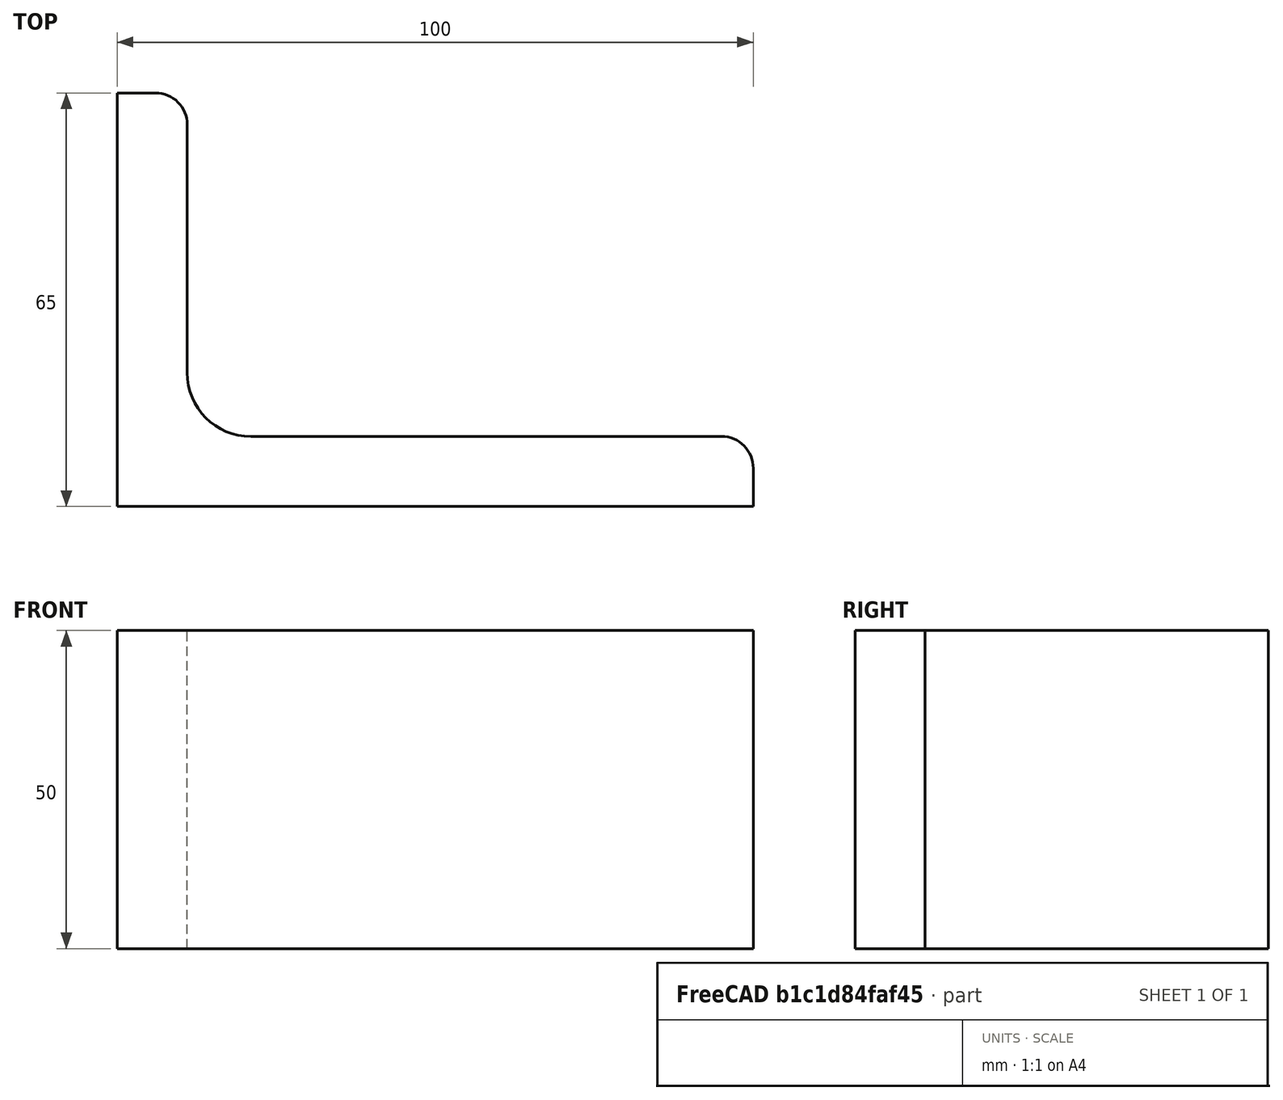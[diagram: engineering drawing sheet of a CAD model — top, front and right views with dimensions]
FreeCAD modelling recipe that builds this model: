
FCSTD DOCUMENT  (FreeCAD 0.15R4671 (Git))
Label: Angle Bar 100x65x11 EN10056 S235JR
License: All rights reserved
LicenseURL: http://en.wikipedia.org/wiki/All_rights_reserved
objects: Sketcher::SketchObject×1, Part::Extrusion×1
note: 2 computed .brp shape members not serialized (recipe doc carries the construction recipe); baked Part::Feature solids carry a one-line shape summary decoded from their .brp

FEATURE [Sketcher::SketchObject] Sketch
  sketch-geometry (9):
    g0: LineSegment StartX=0 StartY=0 StartZ=0 EndX=100 EndY=0 EndZ=0
    g1: LineSegment StartX=100 StartY=0 StartZ=0 EndX=100 EndY=6 EndZ=0
    g2: LineSegment StartX=95 StartY=11 StartZ=0 EndX=21 EndY=11 EndZ=0
    g3: LineSegment StartX=0 StartY=0 StartZ=0 EndX=0 EndY=65 EndZ=0
    g4: LineSegment StartX=0 StartY=65 StartZ=0 EndX=6 EndY=65 EndZ=0
    g5: LineSegment StartX=11 StartY=60 StartZ=0 EndX=11 EndY=21 EndZ=0
    g6: ArcOfCircle CenterX=21 CenterY=21 CenterZ=0 NormalX=0 NormalY=0 NormalZ=1 Radius=10 StartAngle=3.14159 EndAngle=4.71239
    g7: ArcOfCircle CenterX=6 CenterY=60 CenterZ=0 NormalX=0 NormalY=0 NormalZ=1 Radius=5 StartAngle=0 EndAngle=1.5708
    g8: ArcOfCircle CenterX=95 CenterY=6 CenterZ=0 NormalX=0 NormalY=0 NormalZ=1 Radius=5 StartAngle=0 EndAngle=1.5708
  constraints (23):
    c: Coincident(g0,g-1)
    c: Horizontal(g0)
    c: Coincident(g1,g0)
    c: Vertical(g1)
    c: Horizontal(g2)
    c: Coincident(g3,g-1)
    c: Vertical(g3)
    c: Coincident(g4,g3)
    c: Horizontal(g4)
    c: Vertical(g5)
    c: Tangent(g5,g6) = -1.5708
    c: Tangent(g2,g6) = 1.5708
    c: Tangent(g4,g7) = 1.5708
    c: Tangent(g5,g7) = 1.5708
    c: Tangent(g2,g8) = -1.5708
    c: Tangent(g1,g8) = -1.5708
    c: DistanceX(g0) = 100
    c: DistanceY(g3) = 65
    c: DistanceY(g0,g2) = 11
    c: DistanceX(g3,g5) = 11
    c: Radius(g6) = 10
    c: Radius(g8) = 5
    c: Radius(g7) = 5
FEATURE [Part::Extrusion] Extrude  label="Angle Bar 100x65x11 EN10056 S235JR"
  Base = -> Sketch
  Dir = (0,0,50)
  Solid = true
